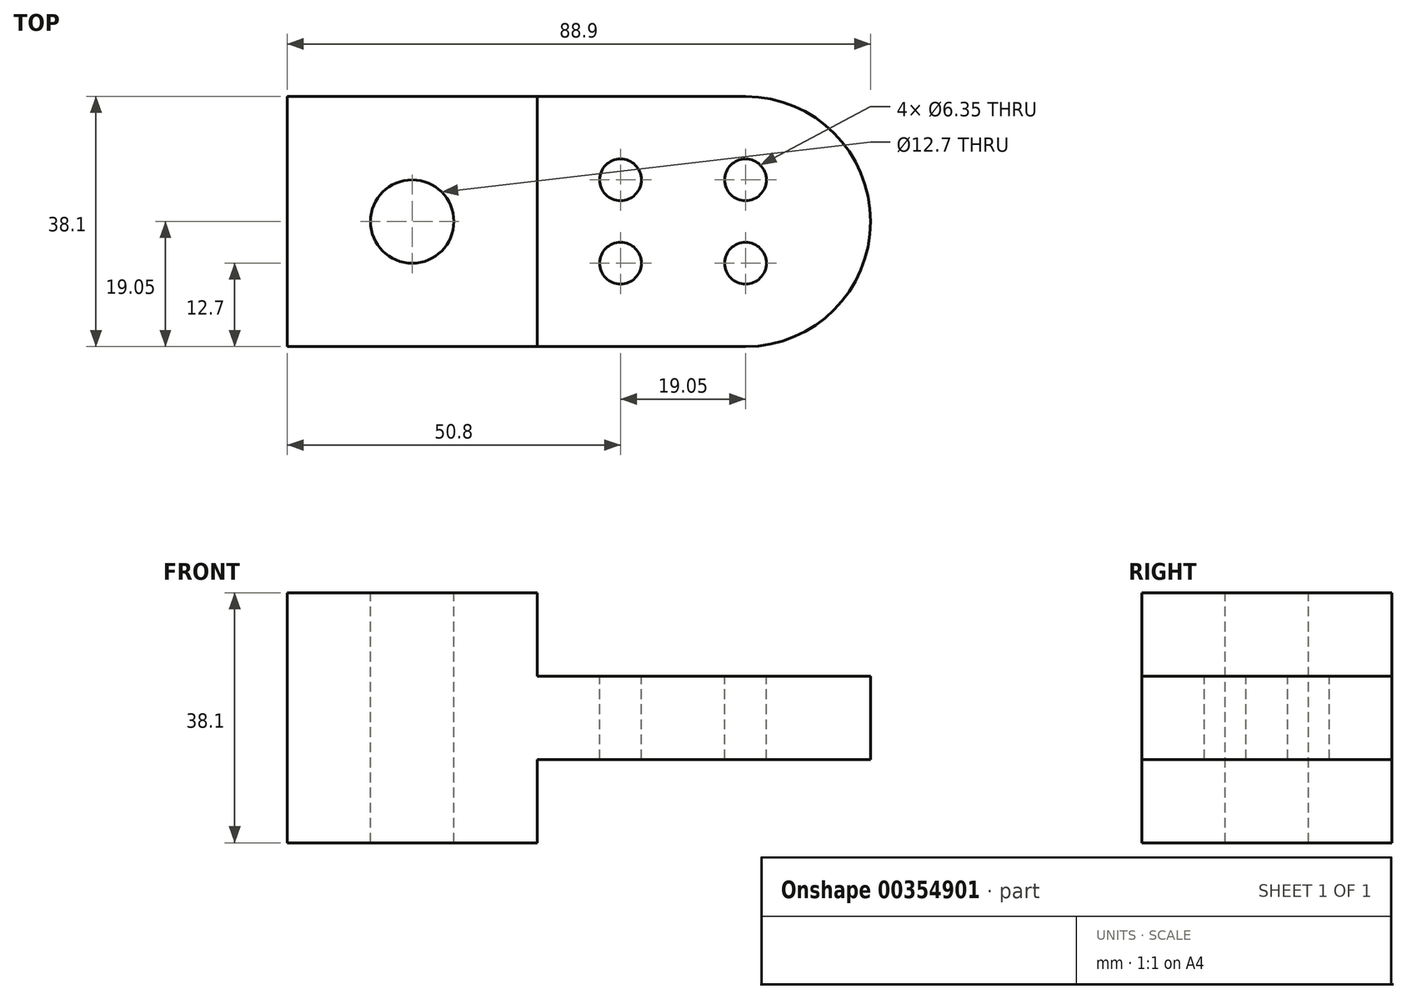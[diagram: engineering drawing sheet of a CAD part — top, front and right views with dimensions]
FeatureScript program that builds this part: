
annotation { "Feature Type Name" : "Feature", "Feature Type Description" : "" }
export const myFeature = defineFeature(function(context is Context, id is Id, definition is map)
    precondition{}
    {
        {
            var Q0;
            Q0=qCreatedBy(makeId("Top.planeOp"),FACE);
            var sketch = newSketch(context, id + "F0", { "sketchPlane" : qUnion([Q0])});
            skLineSegment(sketch, "E0", {"start": v(0, 38.1) * mm, "end": v(0, 0) * mm});
            skLineSegment(sketch, "E1", {"start": v(0, 0) * mm, "end": v(38.1, 0) * mm});
            skLineSegment(sketch, "E2", {"start": v(38.1, 0) * mm, "end": v(38.1, 38.1) * mm});
            skLineSegment(sketch, "E3", {"start": v(38.1, 38.1) * mm, "end": v(0, 38.1) * mm});
            skLineSegment(sketch, "E4", {"start": v(38.1, 38.1) * mm, "end": v(69.85, 38.1) * mm});
            skLineSegment(sketch, "E5", {"start": v(69.85, 0) * mm, "end": v(38.1, 0) * mm});
            skArc(sketch, "E6", {"start": v(69.85, 0) * mm, "mid": v(88.9, 19.05) * mm, "end": v(69.85, 38.1) * mm});
            skSolve(sketch);
        }
        {
            var Q0;
            Q0=makeQuery(id+"F0.imprint","IMPRINT",FACE,{"disambiguationData":[TD([[makeQuery(id+"F0.imprint","IMPRINT",EDGE,{"derivedFrom":sQuery(id+"F0.wireOp",EDGE,"E0")}),1.0]])]});
            extrude(context, id + "F1", {"entities" : qUnion([Q0]), "depth" : 38.1 * mm});
        }
        {
            var Q0;
            Q0=makeQuery(id+"F0.imprint","IMPRINT",FACE,{"disambiguationData":[TD([[makeQuery(id+"F0.imprint","IMPRINT",EDGE,{"derivedFrom":sQuery(id+"F0.wireOp",EDGE,"E2")}),-1.0]])]});
            extrude(context, id + "F2", {"entities" : qUnion([Q0]), "operationType" : NewBodyOperationType.ADD, "depth" : 25.4 * mm});
        }
        {
            var Q0;
            Q0=makeQuery(id+"F2.boolean.opBoolean","MERGE",FACE,{"derivedFrom":[makeQuery(id+"F1.opExtrude","SWEPT_FACE",FACE,{"disambiguationData":[OSD([sQuery(id+"F0.wireOp",EDGE,"E1")])]}),makeQuery(id+"F2.opExtrude","SWEPT_FACE",FACE,{"disambiguationData":[OSD([sQuery(id+"F0.wireOp",EDGE,"E5")])]})]});
            var sketch = newSketch(context, id + "F3", { "sketchPlane" : qUnion([Q0])});
            skLineSegment(sketch, "E7", {"start": v(38.1, 38.1) * mm, "end": v(38.1, 25.4) * mm});
            skLineSegment(sketch, "E8", {"start": v(38.1, 25.4) * mm, "end": v(88.9, 25.4) * mm});
            skLineSegment(sketch, "E9", {"start": v(88.9, 25.4) * mm, "end": v(88.9, 12.7) * mm});
            skLineSegment(sketch, "E10", {"start": v(88.9, 12.7) * mm, "end": v(38.1, 12.7) * mm});
            skLineSegment(sketch, "E11", {"start": v(38.1, 12.7) * mm, "end": v(38.1, 0) * mm});
            skLineSegment(sketch, "E12", {"start": v(38.1, 0) * mm, "end": v(0, 0) * mm});
            skLineSegment(sketch, "E13", {"start": v(0, 0) * mm, "end": v(0, 38.1) * mm});
            skLineSegment(sketch, "E14", {"start": v(0, 38.1) * mm, "end": v(38.1, 38.1) * mm});
            skLineSegment(sketch, "E15", {"start": v(38.1, 0) * mm, "end": v(88.9, 0) * mm});
            skLineSegment(sketch, "E16", {"start": v(88.9, 0) * mm, "end": v(88.9, 12.7) * mm});
            skSolve(sketch);
        }
        {
            var Q0;
            {var subQ0=sQuery(id+"F3.wireOp",EDGE,"E11");Q0=makeQuery(id+"F3.imprint","IMPRINT",FACE,{"disambiguationData":[TD([[makeQuery(id+"F3.imprint","IMPRINT",EDGE,{"derivedFrom":subQ0}),1.0]])]});}
            var Q1;
            {var subQ0=sQuery(id+"F3.wireOp",EDGE,"E16");Q1=makeQuery(id+"F3.imprint","IMPRINT",FACE,{"disambiguationData":[TD([[makeQuery(id+"F3.imprint","IMPRINT",EDGE,{"derivedFrom":subQ0}),1.0]])]});}
            extrude(context, id + "F4", {"entities" : qUnion([Q0, Q1]), "operationType" : NewBodyOperationType.REMOVE, "endBound" : BoundingType.THROUGH_ALL, "oppositeDirection" : true, "depth" : 25.4 * mm});
        }
        {
            var Q0;
            Q0=makeQuery(id+"F1.opExtrude","CAP_FACE",FACE,{"disambiguationData":[OSD([sQuery(id+"F0.wireOp",EDGE,"E0"),sQuery(id+"F0.wireOp",EDGE,"E1"),sQuery(id+"F0.wireOp",EDGE,"E2"),sQuery(id+"F0.wireOp",EDGE,"E3")])],"isStart":false});
            var sketch = newSketch(context, id + "F5", { "sketchPlane" : qUnion([Q0])});
            skCircle(sketch, "E17", {"center": v(19.05, 19.05) * mm, "radius": 6.35 * mm});
            skCircle(sketch, "E18", {"center": v(50.8, 25.4) * mm, "radius": 3.18 * mm});
            skCircle(sketch, "E19", {"center": v(69.85, 25.4) * mm, "radius": 3.18 * mm});
            skCircle(sketch, "E20", {"center": v(50.8, 12.7) * mm, "radius": 3.18 * mm});
            skCircle(sketch, "E21", {"center": v(69.85, 12.7) * mm, "radius": 3.18 * mm});
            skSolve(sketch);
        }
        {
            var Q0;
            Q0=makeQuery(id+"F5.imprint","IMPRINT",FACE,{"disambiguationData":[TD([[makeQuery(id+"F5.imprint","IMPRINT",EDGE,{"derivedFrom":sQuery(id+"F5.wireOp",EDGE,"E17")}),1.0]])]});
            var Q1;
            Q1=makeQuery(id+"F5.imprint","IMPRINT",FACE,{"disambiguationData":[TD([[makeQuery(id+"F5.imprint","IMPRINT",EDGE,{"derivedFrom":sQuery(id+"F5.wireOp",EDGE,"E18")}),1.0]])]});
            var Q2;
            Q2=makeQuery(id+"F5.imprint","IMPRINT",FACE,{"disambiguationData":[TD([[makeQuery(id+"F5.imprint","IMPRINT",EDGE,{"derivedFrom":sQuery(id+"F5.wireOp",EDGE,"E19")}),1.0]])]});
            var Q3;
            Q3=makeQuery(id+"F5.imprint","IMPRINT",FACE,{"disambiguationData":[TD([[makeQuery(id+"F5.imprint","IMPRINT",EDGE,{"derivedFrom":sQuery(id+"F5.wireOp",EDGE,"E21")}),1.0]])]});
            var Q4;
            Q4=makeQuery(id+"F5.imprint","IMPRINT",FACE,{"disambiguationData":[TD([[makeQuery(id+"F5.imprint","IMPRINT",EDGE,{"derivedFrom":sQuery(id+"F5.wireOp",EDGE,"E20")}),1.0]])]});
            extrude(context, id + "F6", {"entities" : qUnion([Q0, Q1, Q2, Q3, Q4]), "operationType" : NewBodyOperationType.REMOVE, "endBound" : BoundingType.THROUGH_ALL, "oppositeDirection" : true, "depth" : 25.4 * mm});
        }
    });
